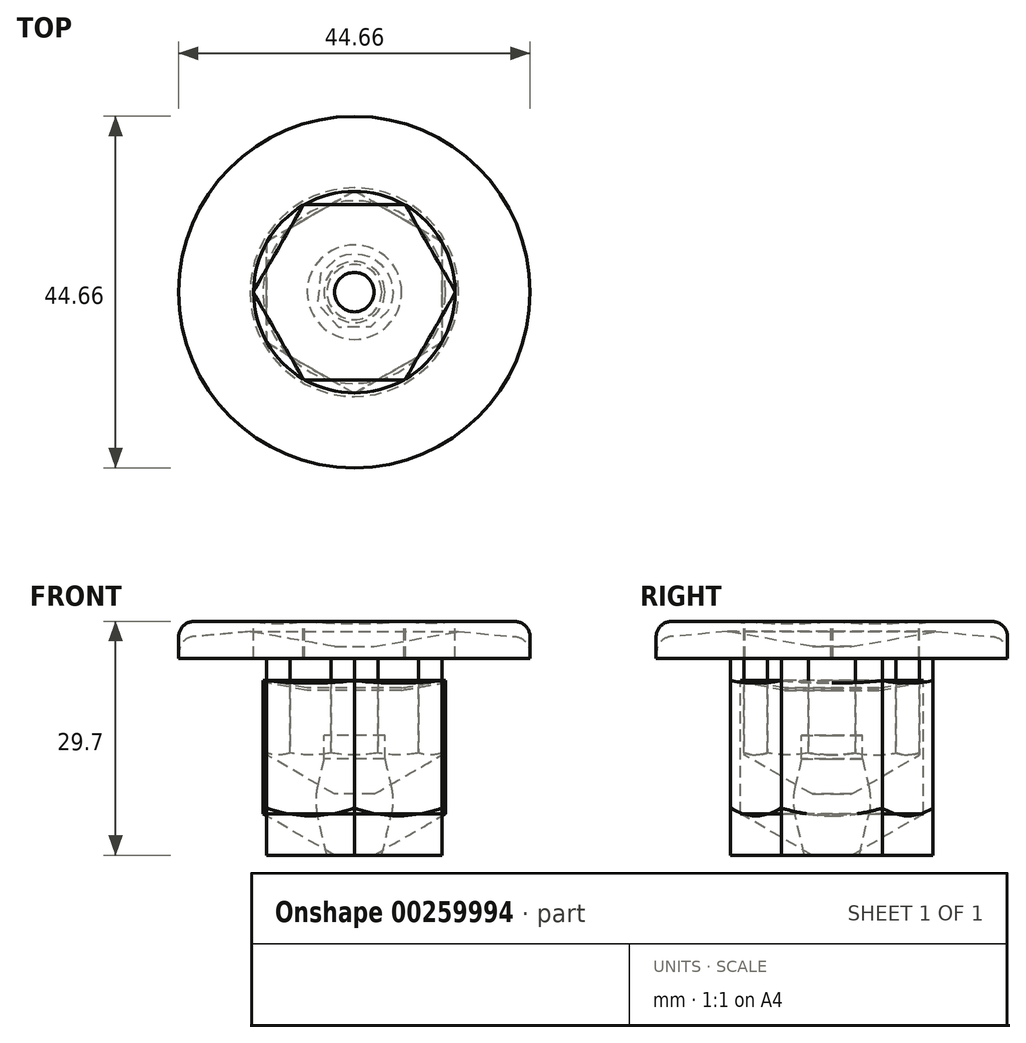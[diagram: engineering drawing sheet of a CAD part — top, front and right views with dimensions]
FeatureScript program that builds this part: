
annotation { "Feature Type Name" : "Feature", "Feature Type Description" : "" }
export const myFeature = defineFeature(function(context is Context, id is Id, definition is map)
    precondition{}
    {
        {
            var Q0;
            Q0=qCreatedBy(makeId("Front.planeOp"),FACE);
            var sketch = newSketch(context, id + "F0", { "sketchPlane" : qUnion([Q0])});
            skLineSegment(sketch, "E0", {"start": v(0, 0) * mm, "end": v(0, 7.75) * mm, "construction": true});
            skLineSegment(sketch, "E1", {"start": v(12.8, 29.7) * mm, "end": v(20.32, 29.7) * mm});
            skLineSegment(sketch, "E2", {"start": v(22.32, 27.7) * mm, "end": v(22.33, 0.33) * mm});
            skLineSegment(sketch, "E3", {"start": v(22, 0) * mm, "end": v(0, 0) * mm});
            skPoint(sketch, "E4.visualSharp", {"position": v(22.32, 29.7) * mm});
            skArc(sketch, "E4.filletArc", {"start": v(22.32, 27.7) * mm, "mid": v(21.74, 29.11) * mm, "end": v(20.32, 29.7) * mm});
            skPoint(sketch, "E5.visualSharp", {"position": v(22.33, 0) * mm});
            skArc(sketch, "E5.filletArc", {"start": v(22, 0) * mm, "mid": v(22.23, 0.1) * mm, "end": v(22.33, 0.33) * mm});
            skLineSegment(sketch, "E6", {"start": v(12.8, 29.7) * mm, "end": v(12.8, 13.7) * mm});
            skLineSegment(sketch, "E7", {"start": v(12.8, 13.7) * mm, "end": v(2.5, 7.75) * mm});
            skLineSegment(sketch, "E8", {"start": v(2.5, 7.75) * mm, "end": v(0, 7.75) * mm});
            skLineSegment(sketch, "E9", {"start": v(0, 7.75) * mm, "end": v(0, 0) * mm});
            skSolve(sketch);
        }
        {
            var Q0;
            Q0=qSketchRegion(id+"F0",true);
            var Q1;
            Q1=sQuery(id+"F0.wireOp",EDGE,"E9");
            revolve(context, id + "F1", {"entities" : qUnion([Q0]), "axis" : qUnion([Q1]), "revolveType" : RevolveType.FULL});
        }
        {
            var Q0;
            Q0=makeQuery(id+"F1.opRevolve","SWEPT_FACE",FACE,{"disambiguationData":[OSD([sQuery(id+"F0.wireOp",EDGE,"E1")])]});
            var sketch = newSketch(context, id + "F2", { "sketchPlane" : qUnion([Q0])});
            skCircle(sketch, "E10", {"center": v(0, 0) * mm, "radius": 20.32 * mm});
            skCircle(sketch, "E11.cCircle", {"center": v(0, 0) * mm, "radius": 11.14 * mm, "construction": true});
            skLineSegment(sketch, "E11.0", {"start": v(-6.43, 11.14) * mm, "end": v(6.43, 11.14) * mm});
            skLineSegment(sketch, "E11.1", {"start": v(6.43, 11.14) * mm, "end": v(12.86, 0) * mm});
            skLineSegment(sketch, "E11.2", {"start": v(12.86, 0) * mm, "end": v(6.43, -11.14) * mm});
            skLineSegment(sketch, "E11.3", {"start": v(6.43, -11.14) * mm, "end": v(-6.43, -11.14) * mm});
            skLineSegment(sketch, "E11.4", {"start": v(-6.43, -11.14) * mm, "end": v(-12.86, 0) * mm});
            skLineSegment(sketch, "E11.5", {"start": v(-12.86, 0) * mm, "end": v(-6.43, 11.14) * mm});
            skPoint(sketch, "E11.0.midPoint", {"position": v(0, 11.14) * mm});
            skSolve(sketch);
        }
        {
            var Q0;
            Q0=qSketchRegion(id+"F2",true);
            var Q1;
            Q1=makeQuery(id+"F1.opRevolve","SWEPT_FACE",FACE,{"disambiguationData":[OSD([sQuery(id+"F0.wireOp",EDGE,"E7")])]});
            extrude(context, id + "F3", {"entities" : qUnion([Q0]), "operationType" : NewBodyOperationType.ADD, "endBound" : BoundingType.UP_TO_SURFACE, "oppositeDirection" : true, "endBoundEntityFace" : qUnion([Q1]), "offsetDistance" : 25 * mm, "depth" : 25 * mm});
        }
        {
            var Q0;
            Q0=makeQuery(id+"F3.boolean.opBoolean","MERGE",FACE,{"derivedFrom":[makeQuery(id+"F1.opRevolve","SWEPT_FACE",FACE,{"disambiguationData":[OSD([sQuery(id+"F0.wireOp",EDGE,"E1")])]}),makeQuery(id+"F3.opExtrude","CAP_FACE",FACE,{"disambiguationData":[OSD([sQuery(id+"F2.wireOp",EDGE,"axiUSiGf-8ymJ-Ezfh-tHsk-ULXXzRlxOoBz"),sQuery(id+"F2.wireOp",EDGE,"WrdyBTnM-XU54-uk96-2Sjo-h1HHDxb1zyqn"),sQuery(id+"F2.wireOp",EDGE,"7iNK7enz-fUzD-7EQp-KRCh-aPKnPlRcPdaK"),sQuery(id+"F2.wireOp",EDGE,"e7c95674-c634-4135-8625-61586754ee6a.1.0"),sQuery(id+"F2.wireOp",EDGE,"e7c95674-c634-4135-8625-61586754ee6a.1.1"),sQuery(id+"F2.wireOp",EDGE,"e7c95674-c634-4135-8625-61586754ee6a.1.2"),sQuery(id+"F2.wireOp",EDGE,"e7c95674-c634-4135-8625-61586754ee6a.2.0"),sQuery(id+"F2.wireOp",EDGE,"e7c95674-c634-4135-8625-61586754ee6a.2.1"),sQuery(id+"F2.wireOp",EDGE,"e7c95674-c634-4135-8625-61586754ee6a.2.2"),sQuery(id+"F2.wireOp",EDGE,"e7c95674-c634-4135-8625-61586754ee6a.3.0"),sQuery(id+"F2.wireOp",EDGE,"e7c95674-c634-4135-8625-61586754ee6a.3.1"),sQuery(id+"F2.wireOp",EDGE,"e7c95674-c634-4135-8625-61586754ee6a.3.2"),sQuery(id+"F2.wireOp",EDGE,"e7c95674-c634-4135-8625-61586754ee6a.4.0"),sQuery(id+"F2.wireOp",EDGE,"e7c95674-c634-4135-8625-61586754ee6a.4.1"),sQuery(id+"F2.wireOp",EDGE,"e7c95674-c634-4135-8625-61586754ee6a.4.2"),sQuery(id+"F2.wireOp",EDGE,"e7c95674-c634-4135-8625-61586754ee6a.5.0"),sQuery(id+"F2.wireOp",EDGE,"e7c95674-c634-4135-8625-61586754ee6a.5.1"),sQuery(id+"F2.wireOp",EDGE,"e7c95674-c634-4135-8625-61586754ee6a.5.2"),sQuery(id+"F2.wireOp",EDGE,"c34f7dbc-1fd9-48ae-9599-0fb72b0d65de.filletArc"),sQuery(id+"F2.wireOp",EDGE,"5fecc0f4-c57f-42b8-a97f-f8fbf54cf4db.filletArc"),sQuery(id+"F2.wireOp",EDGE,"b077568f-b672-48a6-a184-fa18c1575088.filletArc"),sQuery(id+"F2.wireOp",EDGE,"4c4ba650-eb3b-40a6-a5b6-7d0bcd232093.filletArc"),sQuery(id+"F2.wireOp",EDGE,"b016cc09-0b8d-437b-9508-1d7630c9d4ff.filletArc"),sQuery(id+"F2.wireOp",EDGE,"d5479cb3-145b-41e2-b586-5ab3f6452500.filletArc"),sQuery(id+"F2.wireOp",EDGE,"E10")])],"isStart":true})]});
            var sketch = newSketch(context, id + "F4", { "sketchPlane" : qUnion([Q0])});
            skCircle(sketch, "E12", {"center": v(0, 0) * mm, "radius": 12.8 * mm});
            skSolve(sketch);
        }
        {
            var Q0;
            Q0=qSketchRegion(id+"F4",true);
            extrude(context, id + "F5", {"entities" : qUnion([Q0]), "operationType" : NewBodyOperationType.REMOVE, "oppositeDirection" : true, "offsetDistance" : 25 * mm, "depth" : 1 * mm, "hasDraft" : true, "draftAngle" : 80 * degree, "draftPullDirection" : true});
        }
        {
            var Q0;
            Q0=qCreatedBy(makeId("Front.planeOp"),FACE);
            var sketch = newSketch(context, id + "F6", { "sketchPlane" : qUnion([Q0])});
            skLineSegment(sketch, "E13", {"start": v(0, 0) * mm, "end": v(0, 15.2) * mm, "construction": true});
            skLineSegment(sketch, "E14", {"start": v(0, 15.2) * mm, "end": v(3.87, 15.2) * mm});
            skLineSegment(sketch, "E15", {"start": v(3.87, 15.2) * mm, "end": v(3.87, 12.2) * mm});
            skLineSegment(sketch, "E16", {"start": v(3.87, 12.2) * mm, "end": v(4.68, 8.72) * mm});
            skLineSegment(sketch, "E17", {"start": v(3.5, 0) * mm, "end": v(0, 0) * mm});
            skLineSegment(sketch, "E18", {"start": v(0, 15.2) * mm, "end": v(0, 0) * mm});
            skLineSegment(sketch, "E19", {"start": v(3.5, 0) * mm, "end": v(4.68, 5.12) * mm});
            skArc(sketch, "E20.filletArc", {"start": v(4.68, 5.12) * mm, "mid": v(4.88, 6.92) * mm, "end": v(4.68, 8.72) * mm});
            skSolve(sketch);
        }
        {
            var Q0;
            Q0=qSketchRegion(id+"F6",true);
            var Q1;
            Q1=sQuery(id+"F6.wireOp",EDGE,"E18");
            revolve(context, id + "F7", {"entities" : qUnion([Q0]), "axis" : qUnion([Q1]), "revolveType" : RevolveType.FULL});
        }
        {
            var Q0;
            Q0=qCreatedBy(makeId("Front.planeOp"),FACE);
            var sketch = newSketch(context, id + "F8", { "sketchPlane" : qUnion([Q0])});
            skLineSegment(sketch, "E21", {"start": v(0, 0) * mm, "end": v(0, 26.5) * mm});
            skLineSegment(sketch, "E22", {"start": v(22.1, 21.93) * mm, "end": v(19.07, 0.43) * mm});
            skLineSegment(sketch, "E23", {"start": v(18.57, 0) * mm, "end": v(0, 0) * mm});
            skPoint(sketch, "E24.visualSharp", {"position": v(19, 0) * mm});
            skArc(sketch, "E24.filletArc", {"start": v(18.57, 0) * mm, "mid": v(18.9, 0.12) * mm, "end": v(19.07, 0.43) * mm});
            skLineSegment(sketch, "E25", {"start": v(0, 26.5) * mm, "end": v(0, 0) * mm, "construction": true});
            skLineSegment(sketch, "E26", {"start": v(0, 26.5) * mm, "end": v(2.5, 26.5) * mm});
            skLineSegment(sketch, "E27", {"start": v(2.5, 26.5) * mm, "end": v(13.25, 28.4) * mm});
            skLineSegment(sketch, "E28", {"start": v(13.25, 28.4) * mm, "end": v(20.43, 27.77) * mm});
            skArc(sketch, "E29.filletArc", {"start": v(22.1, 21.93) * mm, "mid": v(22.27, 23.91) * mm, "end": v(22.25, 25.9) * mm});
            skPoint(sketch, "E30.visualSharp", {"position": v(22.07, 27.63) * mm});
            skArc(sketch, "E30.filletArc", {"start": v(22.25, 25.9) * mm, "mid": v(21.69, 27.17) * mm, "end": v(20.43, 27.77) * mm});
            skLineSegment(sketch, "E31", {"start": v(22.1, 21.93) * mm, "end": v(22.1, 22) * mm, "construction": true});
            skSolve(sketch);
        }
        {
            var Q0;
            Q0=qSketchRegion(id+"F8",true);
            var Q1;
            Q1=sQuery(id+"F8.wireOp",EDGE,"E21");
            revolve(context, id + "F9", {"entities" : qUnion([Q0]), "axis" : qUnion([Q1]), "revolveType" : RevolveType.FULL});
        }
        {
            var Q0;
            Q0=qCreatedBy(makeId("Front.planeOp"),FACE);
            var sketch = newSketch(context, id + "F10", { "sketchPlane" : qUnion([Q0])});
            skLineSegment(sketch, "E32", {"start": v(0, 0) * mm, "end": v(2.5, 0) * mm});
            skLineSegment(sketch, "E33", {"start": v(2.5, 0) * mm, "end": v(13.3, 6.24) * mm});
            skLineSegment(sketch, "E34", {"start": v(13.3, 6.24) * mm, "end": v(13.3, 22.24) * mm});
            skLineSegment(sketch, "E35", {"start": v(0, 20.95) * mm, "end": v(0, 0) * mm});
            skLineSegment(sketch, "E36", {"start": v(0, 20.95) * mm, "end": v(0, 0) * mm, "construction": true});
            skLineSegment(sketch, "E37", {"start": v(0, 20.95) * mm, "end": v(6, 20.95) * mm});
            skLineSegment(sketch, "E38", {"start": v(6, 20.95) * mm, "end": v(13.3, 22.24) * mm});
            skSolve(sketch);
        }
        {
            var Q0;
            Q0=qSketchRegion(id+"F10",true);
            var Q1;
            Q1=sQuery(id+"F10.wireOp",EDGE,"E35");
            revolve(context, id + "F11", {"surfaceOperationType" : NewSurfaceOperationType.NEW, "entities" : qUnion([Q0]), "axis" : qUnion([Q1]), "revolveType" : RevolveType.FULL});
        }
        {
            var Q0;
            Q0=qCreatedBy(makeId("Top.planeOp"),FACE);
            var sketch = newSketch(context, id + "F12", { "sketchPlane" : qUnion([Q0])});
            skCircle(sketch, "E39.cCircle", {"center": v(0, 0) * mm, "radius": 11.14 * mm, "construction": true});
            skLineSegment(sketch, "E39.0", {"start": v(11.14, 6.43) * mm, "end": v(11.14, -6.43) * mm});
            skLineSegment(sketch, "E39.1", {"start": v(11.14, -6.43) * mm, "end": v(0, -12.86) * mm});
            skLineSegment(sketch, "E39.2", {"start": v(0, -12.86) * mm, "end": v(-11.14, -6.43) * mm});
            skLineSegment(sketch, "E39.3", {"start": v(-11.14, -6.43) * mm, "end": v(-11.14, 6.43) * mm});
            skLineSegment(sketch, "E39.4", {"start": v(-11.14, 6.43) * mm, "end": v(0, 12.86) * mm});
            skLineSegment(sketch, "E39.5", {"start": v(0, 12.86) * mm, "end": v(11.14, 6.43) * mm});
            skPoint(sketch, "E39.0.midPoint", {"position": v(11.14, 0) * mm});
            skCircle(sketch, "E40", {"center": v(0, 0) * mm, "radius": 46.13 * mm});
            skSolve(sketch);
        }
        {
            var Q0;
            Q0=qSketchRegion(id+"F12",true);
            extrude(context, id + "F13", {"entities" : qUnion([Q0]), "operationType" : NewBodyOperationType.REMOVE, "depth" : 25 * mm, "offsetDistance" : 25 * mm});
        }
        {
            var Q0;
            Q0=qCreatedBy(makeId("Front.planeOp"),FACE);
            var sketch = newSketch(context, id + "F14", { "sketchPlane" : qUnion([Q0])});
            skLineSegment(sketch, "E41", {"start": v(0, 0) * mm, "end": v(2.5, 0) * mm});
            skLineSegment(sketch, "E42", {"start": v(2.5, 0) * mm, "end": v(11.6, 5.25) * mm});
            skLineSegment(sketch, "E43", {"start": v(11.6, 5.25) * mm, "end": v(11.6, 22.23) * mm});
            skLineSegment(sketch, "E44", {"start": v(0, 21.24) * mm, "end": v(0, 0) * mm});
            skLineSegment(sketch, "E45", {"start": v(0, 21.24) * mm, "end": v(0, 0) * mm, "construction": true});
            skLineSegment(sketch, "E46", {"start": v(0, 21.24) * mm, "end": v(6, 21.24) * mm});
            skLineSegment(sketch, "E47", {"start": v(6, 21.24) * mm, "end": v(11.6, 22.23) * mm});
            skSolve(sketch);
        }
        {
            var Q0;
            Q0=qSketchRegion(id+"F14",true);
            var Q1;
            Q1=sQuery(id+"F14.wireOp",EDGE,"E44");
            revolve(context, id + "F15", {"surfaceOperationType" : NewSurfaceOperationType.NEW, "entities" : qUnion([Q0]), "axis" : qUnion([Q1]), "revolveType" : RevolveType.FULL});
        }
    });
